# Revit family: Palmshield-Asia-Louver-Panel
name_source: partatom
category: Specialty Equipment
units: mm (PartAtom-declared; Revit-internal decimal feet)

## family parameters
Always vertical = No
Cut with Voids When Loaded = No
Enable Cutting in Views = No
Maintain Annotation Orientation = No
OmniClass Number = 23.55.00.00
OmniClass Title = Manufactured Structures
Part Type = Normal
Room Calculation Point = No
Round Connector Dimension = Use Diameter
Shared = No
Work Plane-Based = No

## types (1)
- Assembly
    Assembly Code = F1020100
    Default Elevation = 0' - 0"
    Description = Asia - Aluminum - Panel Assembly
    Instruction Sheet Link = http://palmshieldlouvers.com
    Keynote = 05 10 00
    Manufacturer = PalmSHIELD
    Material = Metal - PalmSHIELD - Dusty Grey
    Model = Asia - Aluminum - Panel Assembly
    Offset From Surface = 0' - 2"
    Product Documentation Link = http://palmshieldlouvers.com
    Product Page URL = https://palmshieldlouvers.com
    URL = https://palmshieldlouvers.com
    Version = 2020 - v1.0a
    Warranty URL = https://palmshieldlouvers.com

## geometry (parser evidence)
native form markers: Sweep x12
no freeform markers — native parametric forms only
